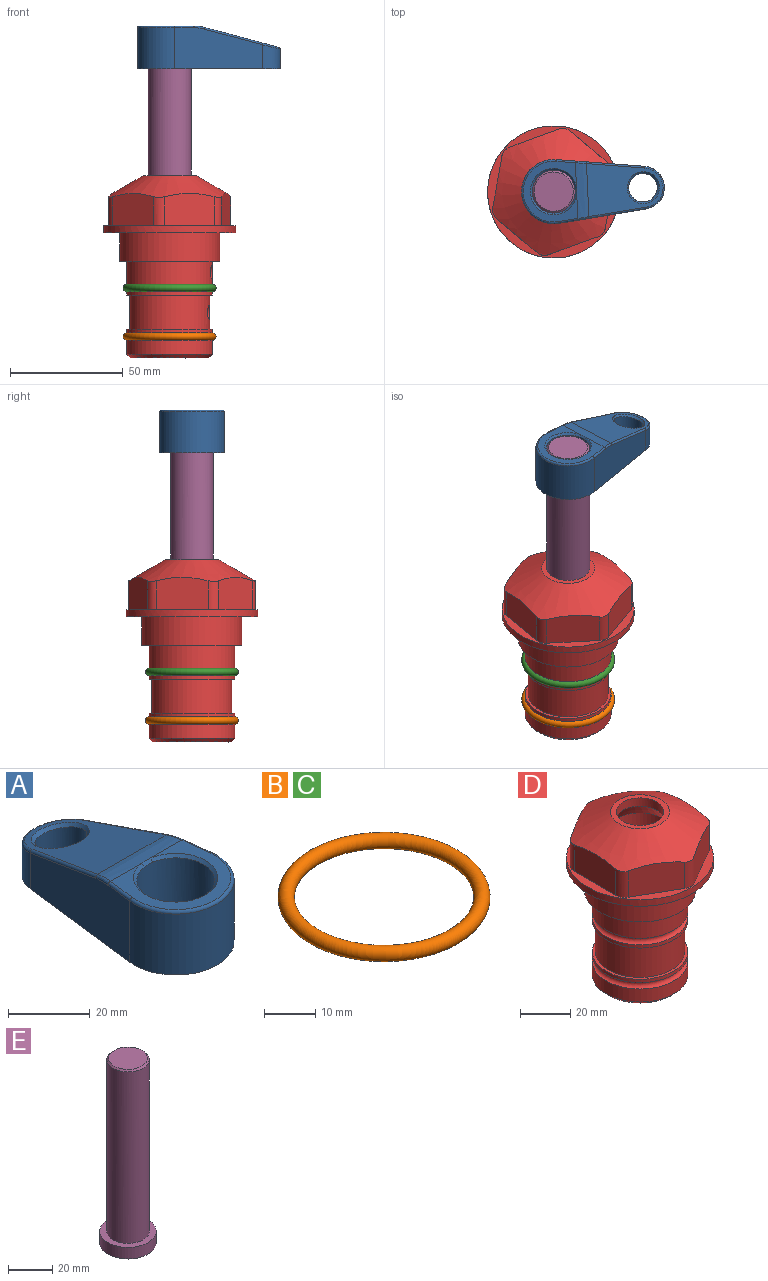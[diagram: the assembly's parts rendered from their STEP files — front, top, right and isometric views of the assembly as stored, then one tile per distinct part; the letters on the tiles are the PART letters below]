
ASSEMBLY  parts=5 mates=4
PART A: 31 faces, bbox 31.7x65.5x19.8 mm
  f0: plane 39.12x18.26mm, normal (0.99,0.12,0), area 612.2mm2, adj f1,f4,f7,f11,f13,f15
  f1: cylinder r=9.53mm len=18.91mm, axis (0,0,-1), area 296.1mm2, adj f0,f2,f7,f17
  f2: plane 39.12x18.26mm, normal (-0.99,0.12,0), area 612.2mm2, adj f1,f4,f7,f12,f14,f16
  f3: cylinder r=6.35mm len=12.7mm, axis (0,0,-1), area 362.4mm2, adj f7,f18
  f4: cylinder r=14.29mm len=28.58mm, axis (0,0,-1), area 882.2mm2, adj f0,f2,f7,f10
  f5: cylinder r=9.53mm len=19.05mm, axis (0,0,-1), area 1092.6mm2, adj f7,f19,f20
  f6: plane 26.99x23.69mm, normal (0,0,1), area 216.2mm2, adj f9,f10,f11,f12,f19
  f7: plane 63.5x28.58mm, normal (0,0,-1), area 661.8mm2, adj f0,f1,f2,f3,f4,f5,f22,f23
  f8: plane 33.52x23.6mm, normal (0,0.26,0.97), area 486mm2, adj f9,f15,f16,f17,f18
  f9: cylinder r=19.05mm len=24.72mm, axis (1,0,0), area 120.4mm2, adj f6,f8,f13,f14,f20
  f10: torus R=13.49mm, axis (0,0,1), area 59mm2, adj f4,f6,f11,f12
  f11: cylinder r=0.79mm len=8.67mm, axis (0.12,-0.99,0), area 10.8mm2, adj f0,f6,f10,f13
  f12: cylinder r=0.79mm len=8.67mm, axis (0.12,0.99,0), area 10.8mm2, adj f2,f6,f10,f14
  f13: bspline ~4.95x1.42mm, area 6.1mm2, adj f0,f9,f11,f15
  f14: bspline ~4.95x1.42mm, area 6.1mm2, adj f2,f9,f12,f16
  f15: cylinder r=0.79mm len=25.95mm, axis (0.12,-0.96,0.26), area 32.9mm2, adj f0,f8,f13,f17
  f16: cylinder r=0.79mm len=25.95mm, axis (0.12,0.96,-0.26), area 32.9mm2, adj f2,f8,f14,f17
  f17: bspline ~18.91x8.38mm, area 30mm2, adj f1,f8,f15,f16
  f18: bspline ~14.29x14.29mm, area 48.3mm2, adj f3,f8
  f19: cone r=9.53mm half-angle=45deg, axis (0,0,1), area 66.5mm2, adj f5,f6,f20
  f20: bspline ~3.22x0.96mm, area 3.5mm2, adj f5,f9,f19
  f21: plane 2.75x2.72mm, normal (0,0,-1), area 2.9mm2, adj f23,f25,f28
  f22: plane 23.05x15.88mm, normal (-0.99,-0.12,0), area 323.6mm2, adj f7,f25,f26,f27,f28,f29
  f23: plane 23.05x15.88mm, normal (0.99,-0.12,0), area 323.6mm2, adj f7,f21,f25,f27,f28,f30
  f24: cylinder r=9.53mm len=10.69mm, axis (0,0,-1), area 114.7mm2, adj f7,f27,f29,f30
  f25: cylinder r=12.7mm len=20.59mm, axis (0,0,-1), area 381.1mm2, adj f7,f21,f22,f23,f26,f28
  f26: plane 2.75x2.72mm, normal (0,0,-1), area 2.9mm2, adj f22,f25,f28
  f27: plane 19.72x18.37mm, normal (0,-0.26,-0.97), area 291.8mm2, adj f22,f23,f24,f28,f29,f30
  f28: cylinder r=15.88mm len=19.92mm, axis (1,0,0), area 54.8mm2, adj f21,f22,f23,f25,f26,f27
  f29: cylinder r=1.59mm len=11mm, axis (0,0,-1), area 34.7mm2, adj f7,f22,f24,f27
  f30: cylinder r=1.59mm len=11mm, axis (0,0,-1), area 34.7mm2, adj f7,f23,f24,f27
PART B: 1 faces, bbox 44.7x44.7x3.2 mm
  f0: torus R=19.05mm, axis (0,0,1), area 1193.9mm2
PART C: same geometry as B
PART D: 36 faces, bbox 58.7x58.7x81 mm
  f0: cylinder r=17.78mm len=35.56mm, axis (0,0,1), area 1670.8mm2, adj f23,f24,f31
  f1: cylinder r=19.05mm len=38.1mm, axis (0,0,1), area 1191.9mm2, adj f26,f27,f30
  f2: plane 58.66x58.66mm, normal (0,0,-1), area 1150.6mm2, adj f3,f28
  f3: cylinder r=29.33mm len=58.66mm, axis (0,0,-1), area 585.1mm2, adj f2,f4
  f4: plane 58.66x58.66mm, normal (0,0,1), area 475.9mm2, adj f3,f5,f6,f7,f8,f9,f10,f11
  f5: plane 20.32x14.34mm, normal (-0.5,0.87,0), area 324.4mm2, adj f4,f15,f16,f17
  f6: plane 20.32x14.34mm, normal (0.5,0.87,0), area 324.4mm2, adj f4,f14,f15,f17
  f7: plane 23.48x14.34mm, normal (1,0,0), area 324.4mm2, adj f4,f13,f14,f17
  f8: plane 20.32x14.34mm, normal (0.5,-0.87,0), area 324.4mm2, adj f4,f12,f13,f17
  f9: plane 20.32x14.34mm, normal (-0.5,-0.87,0), area 324.4mm2, adj f4,f11,f12,f17
  f10: plane 23.48x14.34mm, normal (-1,0,0), area 324.4mm2, adj f4,f11,f16,f17
  f11: cylinder r=5.08mm len=12.85mm, axis (0,0,-1), area 67.2mm2, adj f4,f9,f10,f17
  f12: cylinder r=5.08mm len=12.85mm, axis (0,0,-1), area 67.2mm2, adj f4,f8,f9,f17
  f13: cylinder r=5.08mm len=12.85mm, axis (0,0,-1), area 67.2mm2, adj f4,f7,f8,f17
  f14: cylinder r=5.08mm len=12.85mm, axis (0,0,-1), area 67.2mm2, adj f4,f6,f7,f17
  f15: cylinder r=5.08mm len=12.85mm, axis (0,0,-1), area 67.2mm2, adj f4,f5,f6,f17
  f16: cylinder r=5.08mm len=12.85mm, axis (0,0,-1), area 67.2mm2, adj f4,f5,f10,f17
  f17: cone r=11.73mm half-angle=60deg, axis (0,0,-1), area 2071.8mm2, adj f5,f6,f7,f8,f9,f10,f11,f12
  f18: plane 23.46x23.46mm, normal (0,0,1), area 147.4mm2, adj f17,f35
  f19: plane 34.93x34.93mm, normal (0,0,-1), area 958mm2, adj f29
  f20: cylinder r=19.05mm len=38.1mm, axis (0,0,1), area 760.1mm2, adj f21,f29
  f21: torus R=19.05mm, axis (0,0,1), area 565.3mm2, adj f20,f22
  f22: cylinder r=19.05mm len=38.1mm, axis (0,0,1), area 190mm2, adj f21,f23
  f23: plane 38.1x38.1mm, normal (0,0,1), area 146.9mm2, adj f0,f22
  f24: plane 38.1x38.1mm, normal (0,0,-1), area 146.9mm2, adj f0,f25
  f25: cylinder r=19.05mm len=38.1mm, axis (0,0,1), area 190mm2, adj f24,f26
  f26: torus R=19.05mm, axis (0,0,1), area 565.3mm2, adj f1,f25
  f27: plane 44.45x44.45mm, normal (0,0,-1), area 411.7mm2, adj f1,f28
  f28: cylinder r=22.23mm len=44.45mm, axis (0,0,1), area 1773.5mm2, adj f2,f27
  f29: cone r=19.05mm half-angle=45deg, axis (0,0,1), area 257.5mm2, adj f19,f20
  f30: cylinder r=3.17mm len=6.75mm, axis (-1,0,0), area 128mm2, adj f1,f33
  f31: cylinder r=3.17mm len=6.35mm, axis (-1,0,0), area 102.5mm2, adj f0,f33
  f32: plane 25.4x25.4mm, normal (0,0,1), area 506.7mm2, adj f33
  f33: cylinder r=12.7mm len=66.42mm, axis (0,0,-1), area 5236.2mm2, adj f30,f31,f32,f34
  f34: cone r=9.53mm half-angle=30deg, axis (0,0,-1), area 443.4mm2, adj f33,f35
  f35: cylinder r=9.53mm len=19.05mm, axis (0,0,-1), area 240.9mm2, adj f18,f34
PART E: 6 faces, bbox 25.4x25.4x101.6 mm
  f0: plane 17.46x17.46mm, normal (0,0,1), area 239.5mm2, adj f5
  f1: plane 25.4x25.4mm, normal (0,0,-1), area 506.7mm2, adj f2
  f2: cylinder r=12.7mm len=25.4mm, axis (0,0,1), area 506.7mm2, adj f1,f3
  f3: plane 25.4x25.4mm, normal (0,0,1), area 221.7mm2, adj f2,f4
  f4: cylinder r=9.53mm len=94.46mm, axis (0,0,1), area 5653mm2, adj f3,f5
  f5: cone r=8.73mm half-angle=45deg, axis (0,0,-1), area 64.4mm2, adj f0,f4
PLACE A rot(axis=(0,0,-1),87.4deg) t=(-6.44,4.12,36.12)mm
PLACE B rot(axis=(0,0,-1),10deg) t=(-6.44,4.12,-13.82)mm
PLACE C rot(axis=(0,0,-1),10deg) t=(-6.44,4.12,7.77)mm
PLACE D rot(axis=(0,0,-1),10deg) t=(-6.44,4.12,7.77)mm
PLACE E rot(axis=(0,0,-1),87.4deg) t=(-6.44,4.12,35.32)mm
MATE fastened C.f0 <-> D.f0  axis (0,0,1) through (-6.44,4.12,-16.74)mm
MATE fastened A.f4 <-> E.f2  axis (0,0,-1) through (-6.44,4.12,98.82)mm
MATE cylindrical E.f2 <-> D.f0  axis (0,0,1) through (-6.44,4.12,-2.78)mm
MATE fastened B.f0 <-> D.f0  axis (0,0,1) through (-6.44,4.12,-38.33)mm
